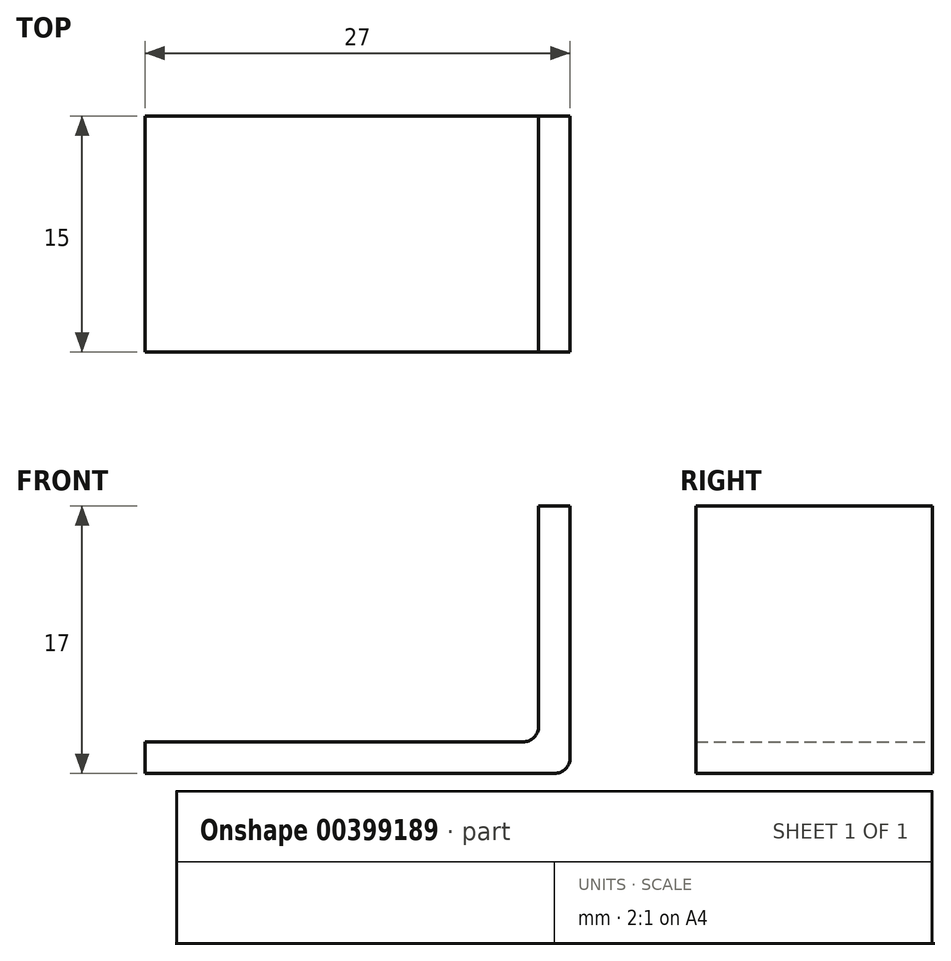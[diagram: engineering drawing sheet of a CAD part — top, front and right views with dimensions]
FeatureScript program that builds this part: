
annotation { "Feature Type Name" : "Feature", "Feature Type Description" : "" }
export const myFeature = defineFeature(function(context is Context, id is Id, definition is map)
    precondition{}
    {
        {
            var Q0;
            Q0=qCreatedBy(makeId("Front.planeOp"),FACE);
            var sketch = newSketch(context, id + "F0", { "sketchPlane" : qUnion([Q0])});
            skLineSegment(sketch, "E0", {"start": v(0, 0) * mm, "end": v(24, 0) * mm});
            skLineSegment(sketch, "E1", {"start": v(25, 1) * mm, "end": v(25, 15) * mm});
            skLineSegment(sketch, "E2", {"start": v(25, 15) * mm, "end": v(27, 15) * mm});
            skLineSegment(sketch, "E3", {"start": v(27, 15) * mm, "end": v(27, 0) * mm});
            skLineSegment(sketch, "E4", {"start": v(27, 0) * mm, "end": v(27, -1) * mm});
            skLineSegment(sketch, "E5", {"start": v(26, -2) * mm, "end": v(0, -2) * mm});
            skLineSegment(sketch, "E6", {"start": v(0, -2) * mm, "end": v(0, 0) * mm});
            skPoint(sketch, "E7.visualSharp", {"position": v(25, 0) * mm});
            skArc(sketch, "E7.filletArc", {"start": v(24, 0) * mm, "mid": v(24.7, 0.3) * mm, "end": v(25, 1) * mm});
            skPoint(sketch, "E8.visualSharp", {"position": v(27, -2) * mm});
            skArc(sketch, "E8.filletArc", {"start": v(26, -2) * mm, "mid": v(26.7, -1.7) * mm, "end": v(27, -1) * mm});
            skSolve(sketch);
        }
        {
            var Q0;
            Q0=makeQuery(id+"F0.imprint","IMPRINT",FACE,{"disambiguationData":[TD([[makeQuery(id+"F0.imprint","IMPRINT",EDGE,{"derivedFrom":sQuery(id+"F0.wireOp",EDGE,"E0")}),-1.0]])]});
            extrude(context, id + "F1", {"entities" : qUnion([Q0]), "depth" : 15 * mm});
        }
    });
